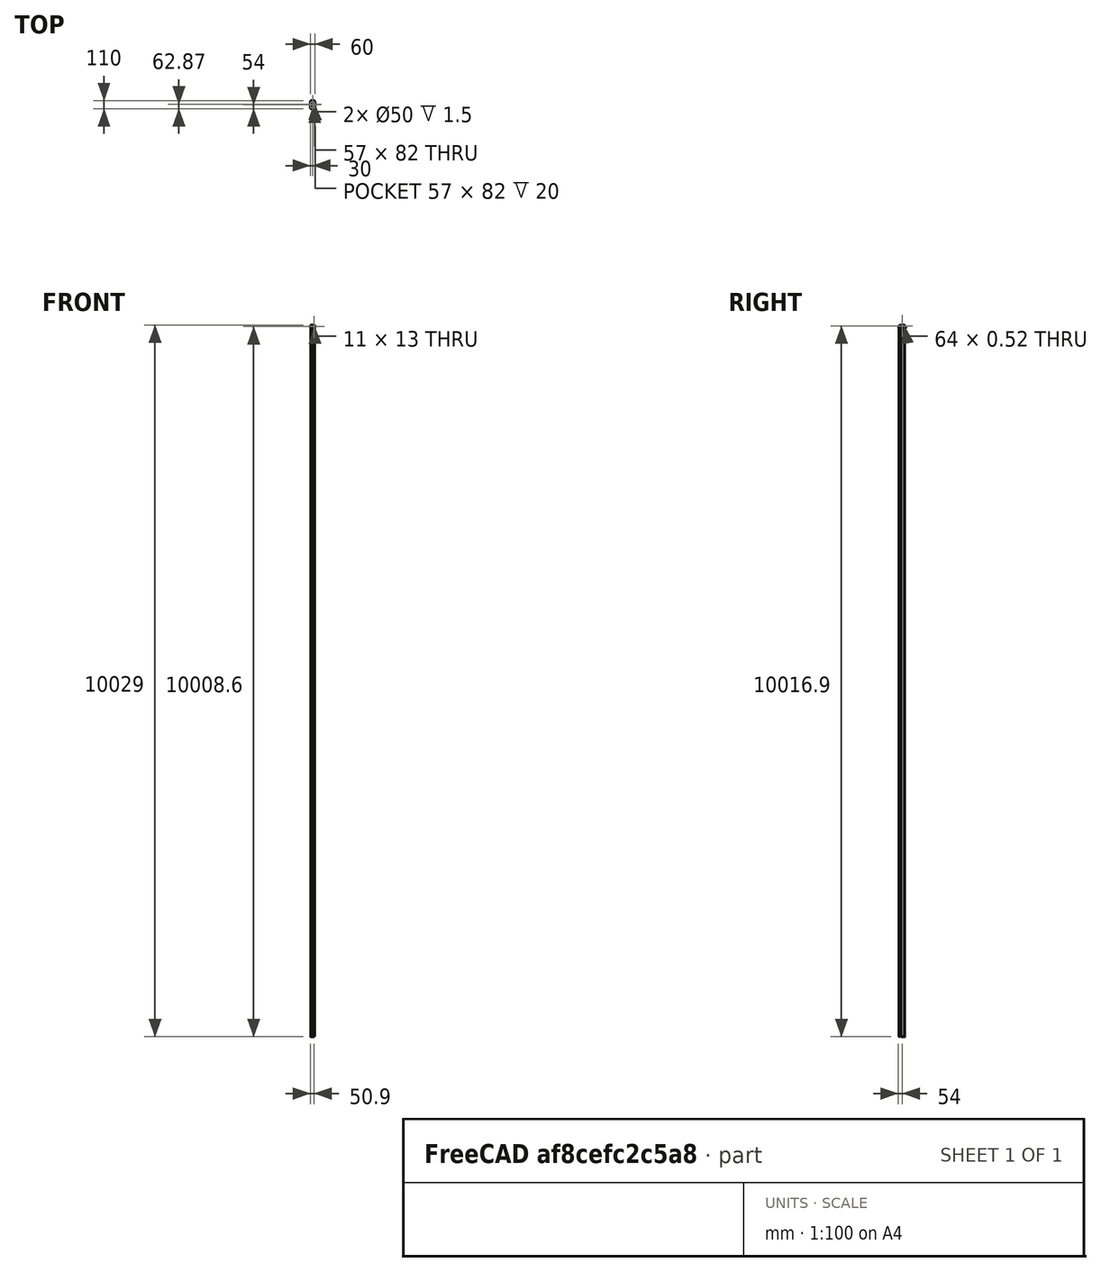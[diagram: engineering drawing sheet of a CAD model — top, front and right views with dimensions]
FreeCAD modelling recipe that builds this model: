
FCSTD DOCUMENT  (FreeCAD 0.16R4751 (Git))
Label: NotifierEnclosurev2_snapfit
License: CC-BY 3.0
LicenseURL: http://creativecommons.org/licenses/by/3.0/
objects: Sketcher::SketchObject×10, Part::Box×7, Part::Cut×6, PartDesign::Pad×5, Part::MultiFuse×5, Part::FeaturePython×4, PartDesign::Pocket×3, App::DocumentObjectGroup×2, Part::Thickness×2, Part::Part2DObjectPython×2, PartDesign::Fillet×2, Part::Offset×2, Part::Fillet×1, Part::Sweep×1
note: 58 computed .brp shape members not serialized (recipe doc carries the construction recipe); baked Part::Feature solids carry a one-line shape summary decoded from their .brp

FEATURE [Part::Box] Box  label="Cube"
  Height = 20
  Length = 57
  Width = 82
FEATURE [Part::Box] Box001  label="Base"
  Height = 1.6
  Length = 54
  Placement = pos=(0,0,3) rot=(0,0,1;0rad)
  Width = 80
FEATURE [Part::Box] Box002  label="EthernetJack"
  Height = 13.6
  Length = 16
  Placement = pos=(11.2,-4.6,4.6) rot=(0,0,1;0rad)
  Width = 21
FEATURE [Part::Box] Box003  label="PowerJack"
  Height = 11
  Length = 9
  Placement = pos=(43.4,-4.5,4.6) rot=(0,0,1;0rad)
  Width = 14.5
FEATURE [Sketcher::SketchObject] Sketch
  ExternalGeometry = -> [Box001]
  Placement = pos=(0,0,4.6) rot=(0,0,1;0rad)
  Support = -> Box001 [Face6]
  sketch-geometry (6):
    g0: Circle CenterX=2.2 CenterY=77.12 CenterZ=0 NormalX=0 NormalY=0 NormalZ=1 Radius=1.5
    g1: Circle CenterX=50.25 CenterY=76.75 CenterZ=0 NormalX=0 NormalY=0 NormalZ=1 Radius=1.5
    g2: Circle CenterX=2 CenterY=2.7 CenterZ=0 NormalX=0 NormalY=0 NormalZ=1 Radius=1.5
    g3: Circle CenterX=39.8 CenterY=2.7 CenterZ=0 NormalX=0 NormalY=0 NormalZ=1 Radius=1.5
    g4: LineSegment [constr] StartX=0.5 StartY=1.2 StartZ=0 EndX=0.5 EndY=5.19188 EndZ=0
    g5: LineSegment [constr] StartX=0.5 StartY=1.2 StartZ=0 EndX=4.53205 EndY=1.2 EndZ=0
  constraints (17):
    c: Radius(g2) = 1.5
    c: Vertical(g4)
    c: Tangent(g4,g2)
    c: Horizontal(g5)
    c: Tangent(g5,g2)
    c: Coincident(g4,g5)
    c: DistanceX(g-1,g4) = 0.5
    c: DistanceY(g-1,g5) = 1.2
    c: Equal(g3,g2)
    c: DistanceY(g-1,g3) = 2.7
    c: DistanceX(g3,g-3) = 14.2
    c: Equal(g0,g1)
    c: Equal(g1,g2)
    c: DistanceY(g0,g-4) = 2.88
    c: DistanceX(g0,g-4) = -2.2
    c: DistanceX(g1,g-4) = 3.75
    c: DistanceY(g1,g-4) = 3.25
FEATURE [PartDesign::Pocket] Pocket  label="Holes"
  Length = 5
  Placement = pos=(0,0,3) rot=(0,0,1;0rad)
  Sketch = -> Sketch
  Type = 1
FEATURE [App::DocumentObjectGroup] Group  label="iBoard"
  Group = -> [Box001,Box002,Box003,Pocket]
FEATURE [Part::Thickness] Thickness
  Faces = -> Box [Face6]
  Intersection = false
  Join = 0
  Mode = 0
  Placement = pos=(-1.5,0,0) rot=(0,0,1;0rad)
  SelfIntersection = false
  Value = 1.5
FEATURE [Sketcher::SketchObject] Sketch001
  ExternalGeometry = -> [Thickness]
  Placement = pos=(-1.5,0,20) rot=(0,0,1;0rad)
  Support = -> Thickness [Face6]
  sketch-geometry (8):
    g0: LineSegment StartX=-1.5 StartY=0 StartZ=0 EndX=-1.5 EndY=82 EndZ=0
    g1: LineSegment StartX=0 StartY=83.5 StartZ=0 EndX=57 EndY=83.5 EndZ=0
    g2: LineSegment StartX=58.5 StartY=0 StartZ=0 EndX=58.5 EndY=82 EndZ=0
    g3: LineSegment StartX=0 StartY=-1.5 StartZ=0 EndX=57 EndY=-1.5 EndZ=0
    g4: ArcOfCircle CenterX=0 CenterY=0 CenterZ=0 NormalX=0 NormalY=0 NormalZ=1 Radius=1.5 StartAngle=3.14159 EndAngle=4.71239
    g5: ArcOfCircle CenterX=0 CenterY=82 CenterZ=0 NormalX=0 NormalY=0 NormalZ=1 Radius=1.5 StartAngle=1.5708 EndAngle=3.14159
    g6: ArcOfCircle CenterX=57 CenterY=82 CenterZ=0 NormalX=0 NormalY=0 NormalZ=1 Radius=1.5 StartAngle=0 EndAngle=1.5708
    g7: ArcOfCircle CenterX=57 CenterY=0 CenterZ=0 NormalX=0 NormalY=0 NormalZ=1 Radius=1.5 StartAngle=4.71239 EndAngle=6.28319
  constraints (24):
    c: Vertical(g0)
    c: Horizontal(g1)
    c: Vertical(g2)
    c: Horizontal(g3)
    c: Coincident(g0,g-10)
    c: Coincident(g0,g-4)
    c: Coincident(g-10,g3)
    c: Coincident(g3,g-9)
    c: Coincident(g2,g-8)
    c: Coincident(g2,g-7)
    c: Coincident(g1,g-6)
    c: Coincident(g1,g-5)
    c: Coincident(g4,g-1)
    c: Coincident(g4,g3)
    c: Coincident(g4,g0)
    c: Coincident(g5,g-3)
    c: Coincident(g5,g0)
    c: Coincident(g5,g1)
    c: Coincident(g6,g-6)
    c: Coincident(g6,g1)
    c: Coincident(g6,g2)
    c: Coincident(g7,g-8)
    c: Coincident(g7,g2)
    c: Coincident(g7,g3)
FEATURE [Part::Part2DObjectPython] Clone2D  label="Clone of Sketch001 (2D)"  # Draft 2D object (typed FeaturePython)
  Objects = -> [Sketch001]
  Placement = pos=(-1.5,0,20) rot=(0,0,1;0rad)
  Scale = (1,1,1)
FEATURE [PartDesign::Pad] Pad
  Length = 1.5
  Length2 = 100
  Placement = pos=(-1.5,0,20) rot=(0,0,1;0rad)
  Sketch = -> Clone2D
  Type = 0
FEATURE [PartDesign::Fillet] Fillet
  Base = -> Pad [Edge22,Edge24,Edge19,Edge13,Edge7,Edge4,Edge16,Edge10]
  Placement = pos=(-1.5,0,20) rot=(0,0,1;0rad)
  Radius = 0.5
FEATURE [Sketcher::SketchObject] Sketch002
  ExternalGeometry = -> [Fillet]
  Placement = pos=(-1.5,0,21.5) rot=(0,0,1;0rad)
  Support = -> Fillet [Face8]
  sketch-geometry (2):
    g0: Circle CenterX=28.5 CenterY=49.8696 CenterZ=0 NormalX=0 NormalY=0 NormalZ=1 Radius=25
    g1: LineSegment [constr] StartX=28.5 StartY=49.8696 StartZ=0 EndX=28.5 EndY=88.1673 EndZ=0
  constraints (4):
    c: Radius(g0) = 25
    c: Coincident(g1,g0)
    c: Vertical(g1)
    c: Symmetric(g-5,g-3,g1)
FEATURE [PartDesign::Pocket] Pocket001
  Length = 5
  Placement = pos=(-1.5,0,20) rot=(0,0,1;0rad)
  Sketch = -> Sketch002
  Type = 1
FEATURE [Sketcher::SketchObject] Sketch003
  Placement = pos=(-1.5,0,0) rot=(0,0,1;0rad)
  Support = -> Thickness [Face5]
  sketch-geometry (4):
    g0: Circle CenterX=3.53528 CenterY=2.63614 CenterZ=0 NormalX=0 NormalY=0 NormalZ=1 Radius=2.5
    g1: Circle CenterX=41.3722 CenterY=2.74074 CenterZ=0 NormalX=0 NormalY=0 NormalZ=1 Radius=2.5
    g2: Circle CenterX=3.78181 CenterY=77.146 CenterZ=0 NormalX=0 NormalY=0 NormalZ=1 Radius=2.5
    g3: Circle CenterX=51.8469 CenterY=76.7239 CenterZ=0 NormalX=0 NormalY=0 NormalZ=1 Radius=2.5
  constraints (4):
    c: Radius(g0) = 2.5
    c: Equal(g0,g1)
    c: Equal(g1,g2)
    c: Equal(g2,g3)
FEATURE [PartDesign::Pad] Pad001
  Length = 3
  Length2 = 100
  Placement = pos=(-1.5,0,0) rot=(0,0,1;0rad)
  Sketch = -> Sketch003
  Type = 0
FEATURE [Sketcher::SketchObject] Sketch004
  ExternalGeometry = -> [Pad001]
  Placement = pos=(-1.5,0,3) rot=(0,0,1;0rad)
  Support = -> Pad001 [Face30]
  sketch-geometry (4):
    g0: Circle CenterX=3.78181 CenterY=77.146 CenterZ=0 NormalX=0 NormalY=0 NormalZ=1 Radius=1.4
    g1: Circle CenterX=51.8469 CenterY=76.7239 CenterZ=0 NormalX=0 NormalY=0 NormalZ=1 Radius=1.4
    g2: Circle CenterX=3.53528 CenterY=2.63614 CenterZ=0 NormalX=0 NormalY=0 NormalZ=1 Radius=1.4
    g3: Circle CenterX=41.3722 CenterY=2.74074 CenterZ=0 NormalX=0 NormalY=0 NormalZ=1 Radius=1.4
  constraints (8):
    c: Coincident(g0,g-3)
    c: Coincident(g1,g-4)
    c: Coincident(g2,g-5)
    c: Coincident(g3,g-6)
    c: Radius(g1) = 1.4
    c: Equal(g1,g0)
    c: Equal(g0,g2)
    c: Equal(g2,g3)
FEATURE [Sketcher::SketchObject] Sketch005
  ExternalGeometry = -> [Pocket001]
  Placement = pos=(-1.5,0,20) rot=(1,0,0;3.14159rad)
  Support = -> Pocket001 [Face4]
  sketch-geometry (8):
    g0: LineSegment StartX=0.2 StartY=-0.2 StartZ=0 EndX=56.8 EndY=-0.2 EndZ=0
    g1: LineSegment StartX=56.8 StartY=-0.2 StartZ=0 EndX=56.8 EndY=-81.8 EndZ=0
    g2: LineSegment StartX=56.8 StartY=-81.8 StartZ=0 EndX=0.2 EndY=-81.8 EndZ=0
    g3: LineSegment StartX=0.2 StartY=-81.8 StartZ=0 EndX=0.2 EndY=-0.2 EndZ=0
    g4: LineSegment StartX=1.5 StartY=-1.5 StartZ=0 EndX=55.5 EndY=-1.5 EndZ=0
    g5: LineSegment StartX=55.5 StartY=-1.5 StartZ=0 EndX=55.5 EndY=-80.5 EndZ=0
    g6: LineSegment StartX=55.5 StartY=-80.5 StartZ=0 EndX=1.5 EndY=-80.5 EndZ=0
    g7: LineSegment StartX=1.5 StartY=-80.5 StartZ=0 EndX=1.5 EndY=-1.5 EndZ=0
  constraints (12):
    c: DistanceX(g-1,g3) = 0.2
    c: DistanceY(g-1,g0) = -0.2
    c: Coincident(g0,g3)
    c: DistanceY(g0,g-3) = 0.2
    c: DistanceX(g1,g-3) = 0.2
    c: Coincident(g1,g0)
    c: DistanceX(g1,g-6) = 0.2
    c: DistanceY(g2,g-6) = -0.2
    c: Coincident(g2,g1)
    c: DistanceX(g3,g-5) = -0.2
    c: DistanceY(g2,g-5) = -0.2
    c: Coincident(g2,g3)
FEATURE [PartDesign::Pad] Pad002
  Length = 2
  Length2 = 100
  Placement = pos=(-1.5,0,20) rot=(0,0,1;0rad)
  Sketch = -> Sketch005
  Type = 0
FEATURE [Part::Offset] Offset
  Fill = false
  Intersection = false
  Join = 2
  Mode = 0
  SelfIntersection = false
  Source = -> Box002
  Value = 1
FEATURE [Part::Offset] Offset001
  Fill = false
  Intersection = false
  Join = 2
  Mode = 0
  SelfIntersection = false
  Source = -> Box003
  Value = 1
FEATURE [Part::MultiFuse] Fusion002
  Shapes = -> [Offset,Offset001]
FEATURE [Part::Cut] Cut002
  Tool = -> Fusion002
FEATURE [Part::Cut] Cut003  label="Lid001"
  Tool = -> Offset
FEATURE [Sketcher::SketchObject] Sketch006
  ExternalGeometry = -> [Cut003]
  Placement = pos=(0,0,21.5) rot=(0,0,1;0rad)
  Support = -> Cut003 [Face60]
  sketch-geometry (1):
    g0: Circle CenterX=27 CenterY=49.8696 CenterZ=0 NormalX=0 NormalY=0 NormalZ=1 Radius=24.5
  constraints (2):
    c: Coincident(g0,g-3)
    c: Radius(g0) = 24.5
FEATURE [Part::Part2DObjectPython] Clone2D001  label="Clone of Sketch006 (2D)"  # Draft 2D object (typed FeaturePython)
  Objects = -> [Sketch006]
  Placement = pos=(0,0,20.5) rot=(0,0,1;0rad)
  Scale = (1,1,1)
FEATURE [PartDesign::Pad] Pad003
  Length = 10
  Length2 = 100
  Placement = pos=(0,0,20.5) rot=(0,0,1;0rad)
  Sketch = -> Clone2D001
  Type = 0
FEATURE [PartDesign::Fillet] Fillet001
  Base = -> Pad003 [Edge3]
  Placement = pos=(0,0,20.5) rot=(0,0,1;0rad)
  Radius = 5
FEATURE [Sketcher::SketchObject] Sketch007
  ExternalGeometry = -> [Fillet001]
  Placement = pos=(0,0,20.5) rot=(1,0,0;3.14159rad)
  Support = -> Fillet001 [Face3]
  sketch-geometry (1):
    g0: Circle CenterX=27 CenterY=-49.8696 CenterZ=0 NormalX=0 NormalY=0 NormalZ=1 Radius=26.5
  constraints (2):
    c: Coincident(g0,g-3)
    c: Radius(g0) = 26.5
FEATURE [PartDesign::Pad] Pad004
  Length = 1.5
  Length2 = 100
  Placement = pos=(0,0,20.5) rot=(0,0,1;0rad)
  Sketch = -> Sketch007
  Type = 0
FEATURE [Part::Thickness] Thickness001
  Faces = -> Pad004 [Face3]
  Intersection = false
  Join = 0
  Mode = 0
  SelfIntersection = false
  Value = -1.5
FEATURE [Part::Box] Box005  label="Cube001"
  Height = 1.5
  Length = 58
  Placement = pos=(-2,-13,-1.5) rot=(0,0,1;0rad)
  Width = 110
FEATURE [Part::Fillet] Fillet002
  Base = -> Box005
  Edges = 4 edges r=5: [Edge1,Edge3,Edge5,Edge7]
FEATURE [Sketcher::SketchObject] Sketch008
  ExternalGeometry = -> [Fillet002]
  Support = -> Fillet002 [Face2]
  sketch-geometry (4):
    g0: Circle CenterX=3 CenterY=92 CenterZ=0 NormalX=0 NormalY=0 NormalZ=1 Radius=1.5
    g1: Circle CenterX=51 CenterY=92 CenterZ=0 NormalX=0 NormalY=0 NormalZ=1 Radius=1.5
    g2: Circle CenterX=3 CenterY=-8 CenterZ=0 NormalX=0 NormalY=0 NormalZ=1 Radius=1.5
    g3: Circle CenterX=51 CenterY=-8 CenterZ=0 NormalX=0 NormalY=0 NormalZ=1 Radius=1.5
  constraints (8):
    c: Radius(g0) = 1.5
    c: Equal(g0,g1)
    c: Equal(g1,g3)
    c: Equal(g3,g2)
    c: Coincident(g2,g-6)
    c: Coincident(g3,g-5)
    c: Coincident(g0,g-3)
    c: Coincident(g1,g-4)
FEATURE [PartDesign::Pocket] Pocket003
  Length = 5
  Sketch = -> Sketch008
  Type = 0
FEATURE [Part::MultiFuse] Fusion003
  Shapes = -> [Cut002,Pocket003]
FEATURE [Part::Cut] Cut004
  Base = -> Fusion003
FEATURE [Sketcher::SketchObject] Sketch009
  ExternalGeometry = -> [Cut003]
  Placement = pos=(0,0.2,0) rot=(1,0,0;1.5708rad)
  Support = -> Cut003 [Face22]
  sketch-geometry (4):
    g0: LineSegment StartX=-1.3 StartY=18.75 StartZ=0 EndX=-1.94952 EndY=18.375 EndZ=0
    g1: LineSegment StartX=-1.94952 StartY=18.375 StartZ=0 EndX=-1.3 EndY=18 EndZ=0
    g2: LineSegment StartX=-1.3 StartY=18 StartZ=0 EndX=-1.3 EndY=18.75 EndZ=0
    g3: Circle [constr] CenterX=-1.51651 CenterY=18.375 CenterZ=0 NormalX=0 NormalY=0 NormalZ=1 Radius=0.433013
  constraints (11):
    c: Coincident(g0,g1)
    c: Coincident(g1,g2)
    c: Coincident(g2,g0)
    c: Equal(g0,g1)
    c: Equal(g0,g2)
    c: PointOnObject(g0,g3)
    c: PointOnObject(g1,g3)
    c: PointOnObject(g2,g3)
    c: Vertical(g2)
    c: DistanceY(g1,g0) = 0.75
    c: Coincident(g1,g-3)
FEATURE [Part::MultiFuse] Fusion004
  Shapes = -> [Cut003]
FEATURE [Part::Sweep] Sweep
  Frenet = false
  Sections = -> [Sketch009]
  Solid = true
  Spine = -> Pad002 [Edge48,Edge49,Edge43,Edge46]
  Transition = 1
FEATURE [Part::MultiFuse] Fusion005
  Shapes = -> [Pad002,Sweep]
FEATURE [Part::Box] Box006  label="Cube002"
  Height = 10
  Length = 10
  Placement = pos=(-2,-1,10) rot=(0,0,1;0rad)
  Width = 10
FEATURE [Part::FeaturePython] Array  # Draft array (typed FeaturePython)
  Angle = 360
  ArrayType = 0
  Axis = (0,0,1)
  Base = -> Box006
  Center = (0,0,0)
  Fuse = false
  IntervalAxis = (0,0,0)
  IntervalX = (48,0,0)
  IntervalY = (0,74,0)
  IntervalZ = (0,0,0)
  NumberPolar = 1
  NumberX = 2
  NumberY = 2
  NumberZ = 1
FEATURE [Part::Cut] Cut005
  Base = -> Fusion005
  Tool = -> Array
FEATURE [Part::Cut] Cut006
  Base = -> Cut004
  Tool = -> Cut005
FEATURE [Part::Cut] Cut
  Base = -> Cut005
  Tool = -> Offset
FEATURE [Part::Box] Box007  label="Cube003"
  Height = 10
  Length = 10
  Placement = pos=(-1,-1.5,8) rot=(0,0,1;0rad)
  Width = 1.5
FEATURE [Part::FeaturePython] Clone  label="Clone of Cube003"  # Draft clone (typed FeaturePython)
  Objects = -> [Box007]
  Placement = pos=(31,-1.5,8) rot=(0,0,1;0rad)
  Scale = (1,1,1)
FEATURE [Part::FeaturePython] Clone001  label="Clone of Cube004"  # Draft clone (typed FeaturePython)
  Objects = -> [Box007]
  Placement = pos=(-1,82,8) rot=(0,0,1;0rad)
  Scale = (1,1,1)
FEATURE [Part::FeaturePython] Clone002  label="Clone of Cube005"  # Draft clone (typed FeaturePython)
  Objects = -> [Box007]
  Placement = pos=(45,82,8) rot=(0,0,1;0rad)
  Scale = (1,1,1)
FEATURE [Part::MultiFuse] Fusion
  Shapes = -> [Cut006,Box007,Clone,Clone001,Clone002]
FEATURE [App::DocumentObjectGroup] Group001  label="Lid"
  Group = -> [Pad,Fillet,Pocket001,Fusion]
